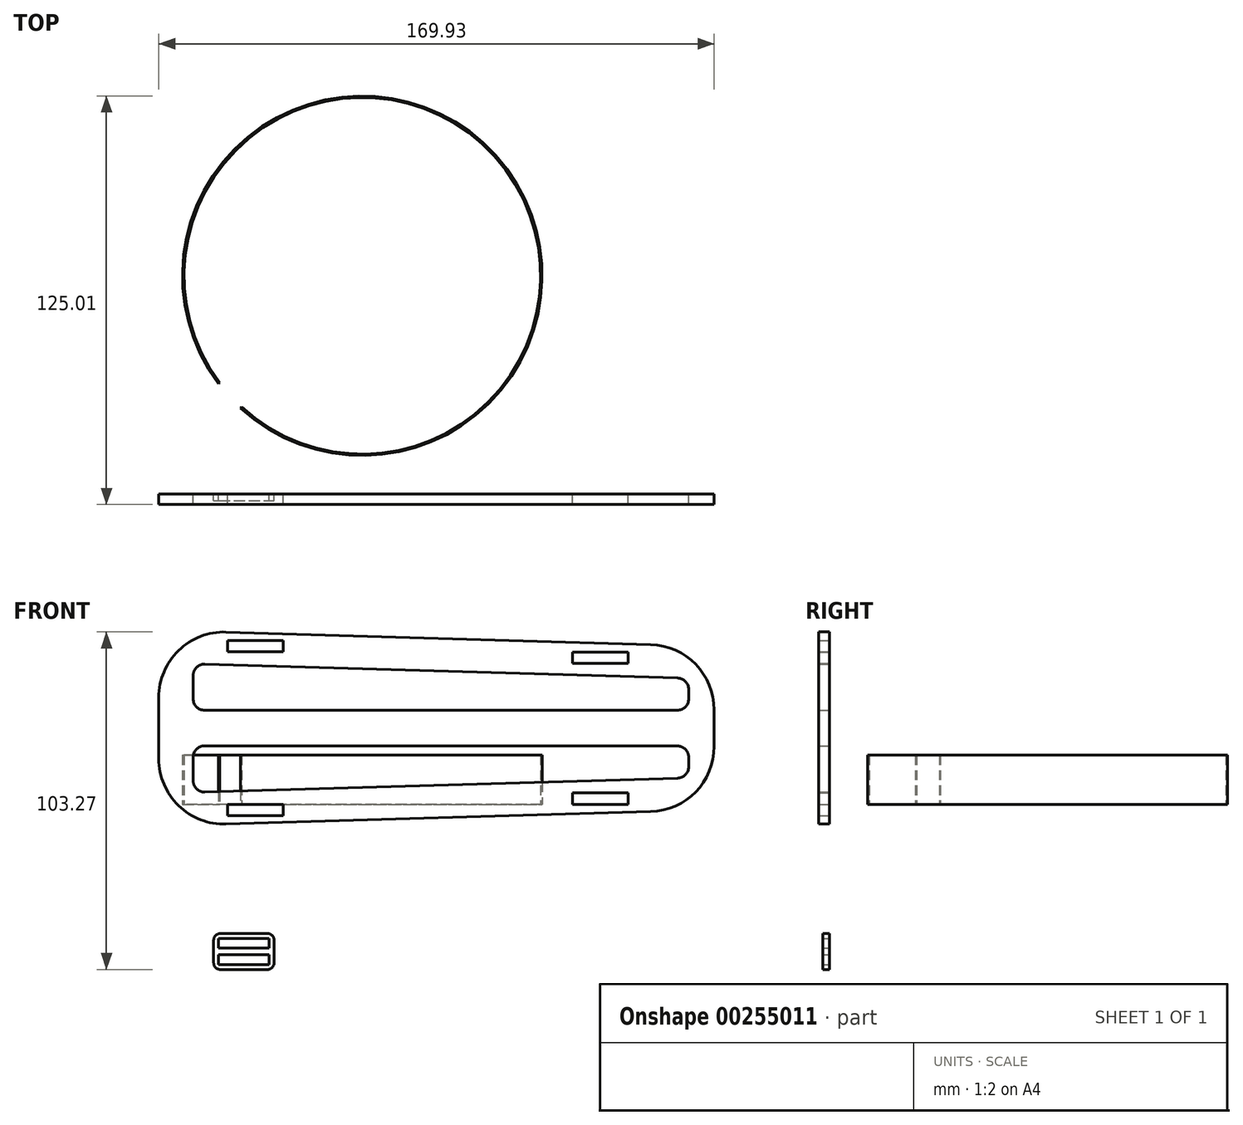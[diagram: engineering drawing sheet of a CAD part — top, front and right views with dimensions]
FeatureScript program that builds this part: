
annotation { "Feature Type Name" : "Feature", "Feature Type Description" : "" }
export const myFeature = defineFeature(function(context is Context, id is Id, definition is map)
    precondition{}
    {
        {
            var Q0;
            Q0=qCreatedBy(makeId("Front.planeOp"),FACE);
            var sketch = newSketch(context, id + "F0", { "sketchPlane" : qUnion([Q0])});
            skLineSegment(sketch, "E0", {"start": v(-64.4, 32.72) * mm, "end": v(-64.4, 13.92) * mm});
            skLineSegment(sketch, "E1", {"start": v(105.53, 17.73) * mm, "end": v(105.53, 28.89) * mm});
            skLineSegment(sketch, "E2", {"start": v(86.12, 48.88) * mm, "end": v(-43.8, 52.71) * mm});
            skLineSegment(sketch, "E3", {"start": v(-43.81, -6.08) * mm, "end": v(86.11, -2.26) * mm});
            skPoint(sketch, "E4.visualSharp", {"position": v(-64.4, 53.32) * mm});
            skArc(sketch, "E4.filletArc", {"start": v(-43.8, 52.71) * mm, "mid": v(-58.33, 47.07) * mm, "end": v(-64.4, 32.72) * mm});
            skPoint(sketch, "E5.visualSharp", {"position": v(-64.4, -6.68) * mm});
            skArc(sketch, "E5.filletArc", {"start": v(-64.4, 13.92) * mm, "mid": v(-58.33, -0.43) * mm, "end": v(-43.81, -6.08) * mm});
            skPoint(sketch, "E6.visualSharp", {"position": v(105.53, -1.7) * mm});
            skArc(sketch, "E6.filletArc", {"start": v(86.11, -2.26) * mm, "mid": v(99.87, 3.8) * mm, "end": v(105.53, 17.73) * mm});
            skPoint(sketch, "E7.visualSharp", {"position": v(105.53, 48.3) * mm});
            skArc(sketch, "E7.filletArc", {"start": v(105.53, 28.89) * mm, "mid": v(99.88, 42.82) * mm, "end": v(86.12, 48.88) * mm});
            skLineSegment(sketch, "E8", {"start": v(-64.4, 23.32) * mm, "end": v(105.53, 23.3) * mm});
            skLineSegment(sketch, "E9", {"start": v(97.72, 35.13) * mm, "end": v(97.72, 32.27) * mm});
            skLineSegment(sketch, "E10", {"start": v(94.22, 28.77) * mm, "end": v(-50.4, 28.77) * mm});
            skLineSegment(sketch, "E11", {"start": v(-53.9, 32.27) * mm, "end": v(-53.9, 39.4) * mm});
            skLineSegment(sketch, "E12", {"start": v(-50.29, 42.9) * mm, "end": v(94.32, 38.63) * mm});
            skLineSegment(sketch, "E13.MirrorCS", {"start": v(94.22, 17.85) * mm, "end": v(-50.4, 17.87) * mm});
            skLineSegment(sketch, "E14.MirrorCS", {"start": v(-53.9, 14.37) * mm, "end": v(-53.9, 7.23) * mm});
            skLineSegment(sketch, "E15.MirrorCS", {"start": v(-50.3, 3.74) * mm, "end": v(94.32, 7.98) * mm});
            skLineSegment(sketch, "E16.MirrorCS", {"start": v(97.72, 11.48) * mm, "end": v(97.72, 14.35) * mm});
            skLineSegment(sketch, "E17.bottom", {"start": v(-43.38, 0) * mm, "end": v(-26.38, 0) * mm});
            skLineSegment(sketch, "E17.top", {"start": v(-43.38, -3.5) * mm, "end": v(-26.38, -3.5) * mm});
            skLineSegment(sketch, "E17.left", {"start": v(-43.38, 0) * mm, "end": v(-43.38, -3.5) * mm});
            skLineSegment(sketch, "E17.right", {"start": v(-26.38, 0) * mm, "end": v(-26.38, -3.5) * mm});
            skLineSegment(sketch, "E18.bottom", {"start": v(62.2, 3.5) * mm, "end": v(79.2, 3.5) * mm});
            skLineSegment(sketch, "E18.top", {"start": v(62.2, 0) * mm, "end": v(79.2, 0) * mm});
            skLineSegment(sketch, "E18.left", {"start": v(62.2, 3.5) * mm, "end": v(62.2, 0) * mm});
            skLineSegment(sketch, "E18.right", {"start": v(79.2, 3.5) * mm, "end": v(79.2, 0) * mm});
            skLineSegment(sketch, "E19.MirrorCS", {"start": v(-26.37, 46.63) * mm, "end": v(-26.37, 50.13) * mm});
            skLineSegment(sketch, "E20.MirrorCS", {"start": v(-43.37, 46.63) * mm, "end": v(-26.37, 46.63) * mm});
            skLineSegment(sketch, "E21.MirrorCS", {"start": v(-43.37, 50.13) * mm, "end": v(-26.37, 50.13) * mm});
            skLineSegment(sketch, "E22.MirrorCS", {"start": v(-43.37, 46.63) * mm, "end": v(-43.37, 50.13) * mm});
            skLineSegment(sketch, "E23.MirrorCS", {"start": v(62.2, 46.62) * mm, "end": v(79.2, 46.62) * mm});
            skLineSegment(sketch, "E24.MirrorCS", {"start": v(62.2, 43.12) * mm, "end": v(62.2, 46.62) * mm});
            skLineSegment(sketch, "E25.MirrorCS", {"start": v(62.2, 43.12) * mm, "end": v(79.2, 43.12) * mm});
            skLineSegment(sketch, "E26.MirrorCS", {"start": v(79.2, 43.12) * mm, "end": v(79.2, 46.62) * mm});
            skPoint(sketch, "E27.visualSharp", {"position": v(-53.9, 43) * mm});
            skArc(sketch, "E27.filletArc", {"start": v(-50.29, 42.9) * mm, "mid": v(-52.83, 41.91) * mm, "end": v(-53.9, 39.4) * mm});
            skPoint(sketch, "E28.visualSharp", {"position": v(-53.9, 28.77) * mm});
            skArc(sketch, "E28.filletArc", {"start": v(-53.9, 32.27) * mm, "mid": v(-52.87, 29.8) * mm, "end": v(-50.4, 28.77) * mm});
            skPoint(sketch, "E29.visualSharp", {"position": v(97.72, 28.77) * mm});
            skArc(sketch, "E29.filletArc", {"start": v(94.22, 28.77) * mm, "mid": v(96.7, 29.8) * mm, "end": v(97.72, 32.27) * mm});
            skPoint(sketch, "E30.visualSharp", {"position": v(97.72, 38.53) * mm});
            skArc(sketch, "E30.filletArc", {"start": v(97.72, 35.13) * mm, "mid": v(96.73, 37.57) * mm, "end": v(94.32, 38.63) * mm});
            skPoint(sketch, "E31.visualSharp", {"position": v(97.72, 17.85) * mm});
            skArc(sketch, "E31.filletArc", {"start": v(97.72, 14.35) * mm, "mid": v(96.7, 16.82) * mm, "end": v(94.22, 17.85) * mm});
            skPoint(sketch, "E32.visualSharp", {"position": v(97.72, 8.08) * mm});
            skArc(sketch, "E32.filletArc", {"start": v(94.32, 7.98) * mm, "mid": v(96.73, 9.04) * mm, "end": v(97.72, 11.48) * mm});
            skPoint(sketch, "E33.visualSharp", {"position": v(-53.9, 17.87) * mm});
            skArc(sketch, "E33.filletArc", {"start": v(-50.4, 17.87) * mm, "mid": v(-52.87, 16.84) * mm, "end": v(-53.9, 14.37) * mm});
            skPoint(sketch, "E34.visualSharp", {"position": v(-53.9, 3.63) * mm});
            skArc(sketch, "E34.filletArc", {"start": v(-53.9, 7.23) * mm, "mid": v(-52.83, 4.72) * mm, "end": v(-50.3, 3.74) * mm});
            skSolve(sketch);
        }
        {
            var Q0;
            Q0=makeQuery(id+"F0.imprint","IMPRINT",FACE,{"disambiguationData":[TD([[makeQuery(id+"F0.imprint","IMPRINT",EDGE,{"derivedFrom":sQuery(id+"F0.wireOp",EDGE,"E2")}),1.0]])]});
            var Q1;
            Q1=makeQuery(id+"F0.imprint","IMPRINT",FACE,{"disambiguationData":[TD([[makeQuery(id+"F0.imprint","IMPRINT",EDGE,{"derivedFrom":sQuery(id+"F0.wireOp",EDGE,"E3")}),1.0]])]});
            extrude(context, id + "F1", {"entities" : qUnion([Q0, Q1]), "depth" : 3.2 * mm});
        }
        {
            var Q0;
            Q0=qCreatedBy(makeId("Front.planeOp"),FACE);
            var sketch = newSketch(context, id + "F2", { "sketchPlane" : qUnion([Q0])});
            skLineSegment(sketch, "E35.bottom", {"start": v(-46.12, -46.05) * mm, "end": v(-30.62, -46.05) * mm});
            skLineSegment(sketch, "E35.top", {"start": v(-46.12, -49.05) * mm, "end": v(-30.62, -49.05) * mm});
            skLineSegment(sketch, "E35.left", {"start": v(-46.12, -46.05) * mm, "end": v(-46.12, -49.05) * mm});
            skLineSegment(sketch, "E35.right", {"start": v(-30.62, -46.05) * mm, "end": v(-30.62, -49.05) * mm});
            skLineSegment(sketch, "E36.bottom", {"start": v(-46.12, -44.05) * mm, "end": v(-30.62, -44.05) * mm});
            skLineSegment(sketch, "E36.top", {"start": v(-46.12, -41.05) * mm, "end": v(-30.62, -41.05) * mm});
            skLineSegment(sketch, "E36.left", {"start": v(-46.12, -44.05) * mm, "end": v(-46.12, -41.05) * mm});
            skLineSegment(sketch, "E36.right", {"start": v(-30.62, -44.05) * mm, "end": v(-30.62, -41.05) * mm});
            skLineSegment(sketch, "E37.bottom", {"start": v(-45.62, -39.55) * mm, "end": v(-31.12, -39.55) * mm});
            skLineSegment(sketch, "E37.top", {"start": v(-45.62, -50.55) * mm, "end": v(-31.12, -50.55) * mm});
            skLineSegment(sketch, "E37.left", {"start": v(-47.62, -41.55) * mm, "end": v(-47.62, -48.55) * mm});
            skLineSegment(sketch, "E37.right", {"start": v(-29.12, -41.55) * mm, "end": v(-29.12, -48.55) * mm});
            skPoint(sketch, "E38.visualSharp", {"position": v(-47.62, -39.55) * mm});
            skArc(sketch, "E38.filletArc", {"start": v(-45.62, -39.55) * mm, "mid": v(-47.03, -40.14) * mm, "end": v(-47.62, -41.55) * mm});
            skPoint(sketch, "E39.visualSharp", {"position": v(-47.62, -50.55) * mm});
            skArc(sketch, "E39.filletArc", {"start": v(-47.62, -48.55) * mm, "mid": v(-47.03, -49.97) * mm, "end": v(-45.62, -50.55) * mm});
            skPoint(sketch, "E40.visualSharp", {"position": v(-29.12, -50.55) * mm});
            skArc(sketch, "E40.filletArc", {"start": v(-31.12, -50.55) * mm, "mid": v(-29.7, -49.97) * mm, "end": v(-29.12, -48.55) * mm});
            skPoint(sketch, "E41.visualSharp", {"position": v(-29.12, -39.55) * mm});
            skArc(sketch, "E41.filletArc", {"start": v(-29.12, -41.55) * mm, "mid": v(-29.7, -40.14) * mm, "end": v(-31.12, -39.55) * mm});
            skSolve(sketch);
        }
        {
            var Q0;
            Q0=makeQuery(id+"F2.imprint","IMPRINT",FACE,{"disambiguationData":[TD([[makeQuery(id+"F2.imprint","IMPRINT",EDGE,{"derivedFrom":sQuery(id+"F2.wireOp",EDGE,"E35.bottom")}),1.0]])]});
            extrude(context, id + "F3", {"entities" : qUnion([Q0]), "depth" : 2 * mm});
        }
        {
            var Q0;
            Q0=qCreatedBy(makeId("Top.planeOp"),FACE);
            var sketch = newSketch(context, id + "F4", { "sketchPlane" : qUnion([Q0])});
            skArc(sketch, "E42", {"start": v(-39.4, 26.35) * mm, "mid": v(38.65, 103.7) * mm, "end": v(-46.1, 33.77) * mm});
            skArc(sketch, "E43.0", {"start": v(-39.1, 26.68) * mm, "mid": v(38.31, 103.4) * mm, "end": v(-45.75, 34.04) * mm});
            skLineSegment(sketch, "E44", {"start": v(-45.75, 34.04) * mm, "end": v(-46.1, 33.77) * mm});
            skLineSegment(sketch, "E45", {"start": v(-39.1, 26.68) * mm, "end": v(-39.4, 26.35) * mm});
            skSolve(sketch);
        }
        {
            var Q0;
            Q0 = qSketchRegion(id + "F4", true);
            extrude(context, id + "F5", {"entities" : qUnion([Q0]), "depth" : 15 * mm});
        }
    });
